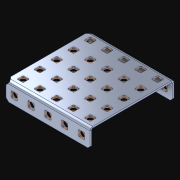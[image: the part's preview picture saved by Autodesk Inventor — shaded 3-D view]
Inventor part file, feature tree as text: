
AUTODESK INVENTOR PART (.ipt)
format: ipt  version: 2021 (Build 250183000, 183)  size: 1,476,608 bytes
history: native  units: in
note: dims shown in document units (in); Inventor stores cm internally (conversion verified against a paired STEP export)
features: extrude x36, other x36, sketch x4, pattern_linear x3
ambient origin geometry x8: Origin, YZ Plane, XZ Plane, XY Plane, X Axis, Y Axis, Z Axis, Center Point
bodies: Solid1 (feature_tree)
feature tree (79):
  pattern_linear  "Rectangular Pattern1"  Spacing1=0.182in  [1 undecoded]
  pattern_linear  "Rectangular Pattern2"  Spacing1=0.046in  [1 undecoded]
  pattern_linear  "Rectangular Pattern3"  Spacing1=0.5in  [1 undecoded]
  extrude  "Extrusion1"  Depth=0.046in
  sketch  "Sketch1"  dims[d0=0.182in]
  other  "Srf1"
  sketch  "Sketch2"  dims[d1=0.046in d2=0.0in]
  other  "Srf2"
  sketch  "Sketch3"  dims[d3=0.182in]
  other  "Srf3"
  other  "Srf4"
  other  "Srf5"
  other  "Srf6"
  other  "Srf7"
  other  "Srf38"
  other  "Srf39"
  other  "Srf40"
  other  "Srf41"
  other  "Srf72"
  other  "Srf73"
  other  "Srf74"
  other  "Srf75"
  other  "Srf76"
  other  "Srf107"
  other  "Srf108"
  other  "Srf109"
  other  "Srf110"
  other  "Srf111"
  other  "Srf142"
  other  "Srf143"
  other  "Srf144"
  other  "Srf145"
  other  "Srf146"
  other  "Srf177"
  other  "Srf178"
  other  "Srf179"
  other  "Srf180"
  other  "Srf181"
  other  "Srf212"
  other  "Srf213"
  other  "Srf214"
  other  "Srf215"
  sketch  "Sketch4"  dims[d4=0.046in d5=0.0in d6=0.182in d7=0.046in d8=0.0in d11=0.5in d12=1.9685in d14=0.5in d15=1.9685in d17=0.5in d18=1.9685in d20=0.5in d21=15.0in d22=0.0in]
  parser-record x1  (decoder bookkeeping rows leaked as tree rows — omitted from the tree; the rows remain in map.json)
  extrude  "ExtrusionSrf1"  Depth=0.046in
  extrude  "ExtrusionSrf2"  Depth=0.046in
  extrude  "ExtrusionSrf3"  Depth=0.046in
  extrude  "ExtrusionSrf4"  Depth=0.046in
  extrude  "ExtrusionSrf5"  Depth=0.046in
  extrude  "ExtrusionSrf6"  TaperAngle=0.0deg  [1 undecoded]
  extrude  "ExtrusionSrf7"  [1 undecoded]
  extrude  "ExtrusionSrf38"  [1 undecoded]
  extrude  "ExtrusionSrf39"  [1 undecoded]
  extrude  "ExtrusionSrf40"  [1 undecoded]
  extrude  "ExtrusionSrf41"  [1 undecoded]
  extrude  "ExtrusionSrf72"  [1 undecoded]
  extrude  "ExtrusionSrf73"  [1 undecoded]
  extrude  "ExtrusionSrf74"  [1 undecoded]
  extrude  "ExtrusionSrf75"  [1 undecoded]
  extrude  "ExtrusionSrf76"  [1 undecoded]
  extrude  "ExtrusionSrf107"  [1 undecoded]
  extrude  "ExtrusionSrf108"  [1 undecoded]
  extrude  "ExtrusionSrf109"  [1 undecoded]
  extrude  "ExtrusionSrf110"  [1 undecoded]
  extrude  "ExtrusionSrf111"  [1 undecoded]
  extrude  "ExtrusionSrf142"  [1 undecoded]
  extrude  "ExtrusionSrf143"  [1 undecoded]
  extrude  "ExtrusionSrf144"  [1 undecoded]
  extrude  "ExtrusionSrf145"  [1 undecoded]
  extrude  "ExtrusionSrf146"  [1 undecoded]
  extrude  "ExtrusionSrf177"  [1 undecoded]
  extrude  "ExtrusionSrf178"  [1 undecoded]
  extrude  "ExtrusionSrf179"  [1 undecoded]
  extrude  "ExtrusionSrf180"  [1 undecoded]
  extrude  "ExtrusionSrf181"  [1 undecoded]
  extrude  "ExtrusionSrf212"  [1 undecoded]
  extrude  "ExtrusionSrf213"  [1 undecoded]
  extrude  "ExtrusionSrf214"  [1 undecoded]
  extrude  "ExtrusionSrf215"  [1 undecoded]
note: 33 required parameter values undecoded (feature->parameter linkage not recoverable at this tier; creation-order binding heuristic only, values carry confidence <= 0.55)
